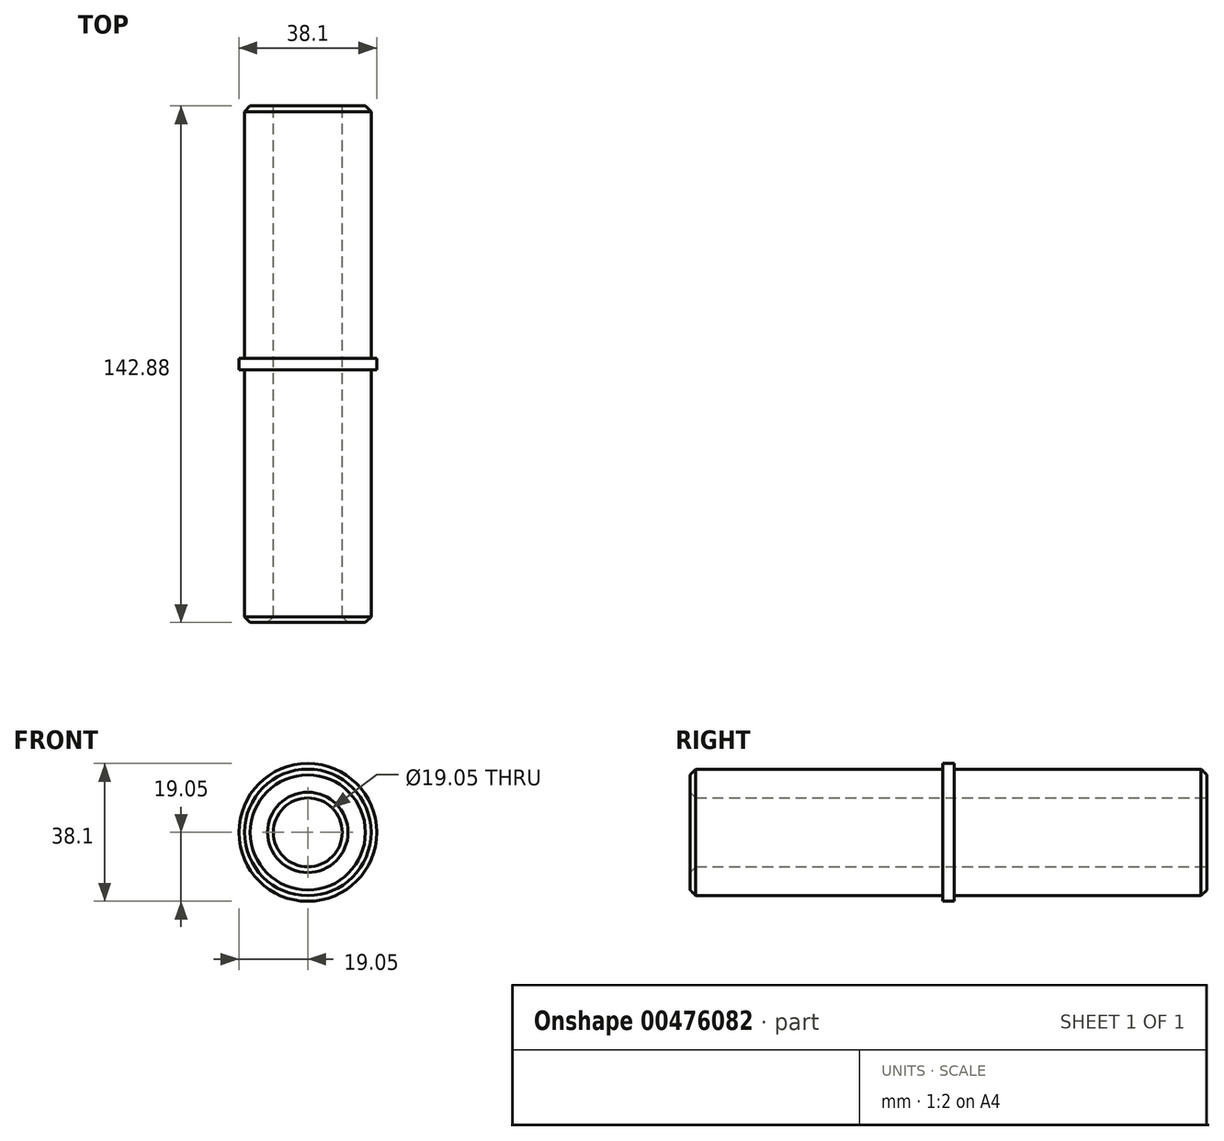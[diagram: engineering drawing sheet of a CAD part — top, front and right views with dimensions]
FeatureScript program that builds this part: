
annotation { "Feature Type Name" : "Feature", "Feature Type Description" : "" }
export const myFeature = defineFeature(function(context is Context, id is Id, definition is map)
    precondition{}
    {
        {
            var Q0;
            Q0=qCreatedBy(makeId("Front.planeOp"),FACE);
            var sketch = newSketch(context, id + "F0", { "sketchPlane" : qUnion([Q0])});
            skCircle(sketch, "E0", {"center": v(0, 0) * mm, "radius": 19.05 * mm});
            skSolve(sketch);
        }
        {
            var Q0;
            Q0=makeQuery(id+"F0.imprint","IMPRINT",FACE,{"disambiguationData":[TD([[makeQuery(id+"F0.imprint","IMPRINT",EDGE,{"derivedFrom":sQuery(id+"F0.wireOp",EDGE,"E0")}),1.0]])]});
            extrude(context, id + "F1", {"entities" : qUnion([Q0]), "depth" : 3.17 * mm});
        }
        {
            var Q0;
            Q0=makeQuery(id+"F1.opExtrude","CAP_FACE",FACE,{"disambiguationData":[OSD([sQuery(id+"F0.wireOp",EDGE,"E0")])],"isStart":false});
            var sketch = newSketch(context, id + "F2", { "sketchPlane" : qUnion([Q0])});
            skCircle(sketch, "E1", {"center": v(0, 0) * mm, "radius": 17.5 * mm});
            skSolve(sketch);
        }
        {
            var Q0;
            Q0=makeQuery(id+"F2.imprint","IMPRINT",FACE,{"disambiguationData":[TD([[makeQuery(id+"F2.imprint","IMPRINT",EDGE,{"derivedFrom":sQuery(id+"F2.wireOp",EDGE,"E1")}),1.0]])]});
            extrude(context, id + "F3", {"entities" : qUnion([Q0]), "operationType" : NewBodyOperationType.ADD, "depth" : 69.85 * mm});
        }
        {
            var Q0;
            Q0=makeQuery(id+"F1.opExtrude","CAP_FACE",FACE,{"disambiguationData":[OSD([sQuery(id+"F0.wireOp",EDGE,"E0")])],"isStart":true});
            var sketch = newSketch(context, id + "F4", { "sketchPlane" : qUnion([Q0])});
            skCircle(sketch, "E2", {"center": v(0, 0) * mm, "radius": 17.5 * mm});
            skSolve(sketch);
        }
        {
            var Q0;
            Q0=makeQuery(id+"F4.imprint","IMPRINT",FACE,{"disambiguationData":[TD([[makeQuery(id+"F4.imprint","IMPRINT",EDGE,{"derivedFrom":sQuery(id+"F4.wireOp",EDGE,"E2")}),1.0]])]});
            extrude(context, id + "F5", {"entities" : qUnion([Q0]), "operationType" : NewBodyOperationType.ADD, "depth" : 69.85 * mm});
        }
        {
            var Q0;
            Q0=makeQuery(id+"F5.opExtrude","CAP_FACE",FACE,{"disambiguationData":[OSD([sQuery(id+"F4.wireOp",EDGE,"E2")])],"isStart":false});
            var sketch = newSketch(context, id + "F6", { "sketchPlane" : qUnion([Q0])});
            skCircle(sketch, "E3", {"center": v(0, 0) * mm, "radius": 9.53 * mm});
            skSolve(sketch);
        }
        {
            var Q0;
            Q0=makeQuery(id+"F6.imprint","IMPRINT",FACE,{"disambiguationData":[TD([[makeQuery(id+"F6.imprint","IMPRINT",EDGE,{"derivedFrom":sQuery(id+"F6.wireOp",EDGE,"E3")}),1.0]])]});
            extrude(context, id + "F7", {"entities" : qUnion([Q0]), "operationType" : NewBodyOperationType.REMOVE, "endBound" : BoundingType.THROUGH_ALL, "oppositeDirection" : true, "depth" : 25.4 * mm});
        }
        {
            var Q0;
            Q0=makeQuery(id+"F3.opExtrude","CAP_EDGE",EDGE,{"disambiguationData":[OSD([sQuery(id+"F2.wireOp",EDGE,"E1")])],"isStart":false});
            var Q1;
            Q1=makeQuery(id+"F7.boolean.opBoolean","INTERSECT",EDGE,{"derivedFrom":[makeQuery(id+"F3.opExtrude","CAP_FACE",FACE,{"disambiguationData":[OSD([sQuery(id+"F2.wireOp",EDGE,"E1")])],"isStart":false}),makeQuery(id+"F7.opExtrude","SWEPT_FACE",FACE,{"disambiguationData":[OSD([sQuery(id+"F6.wireOp",EDGE,"E3")])]})]});
            var Q2;
            Q2=makeQuery(id+"F7.boolean.opBoolean","COPY",EDGE,{"derivedFrom":makeQuery(id+"F7.opExtrude","CAP_EDGE",EDGE,{"disambiguationData":[OSD([sQuery(id+"F6.wireOp",EDGE,"E3")])],"isStart":true})});
            var Q3;
            Q3=makeQuery(id+"F5.opExtrude","CAP_EDGE",EDGE,{"disambiguationData":[OSD([sQuery(id+"F4.wireOp",EDGE,"E2")])],"isStart":false});
            chamfer(context, id + "F8", {"entities" : qUnion([Q0, Q1, Q2, Q3]), "width" : 1.59 * mm, "tangentPropagation" : true});
        }
    });
